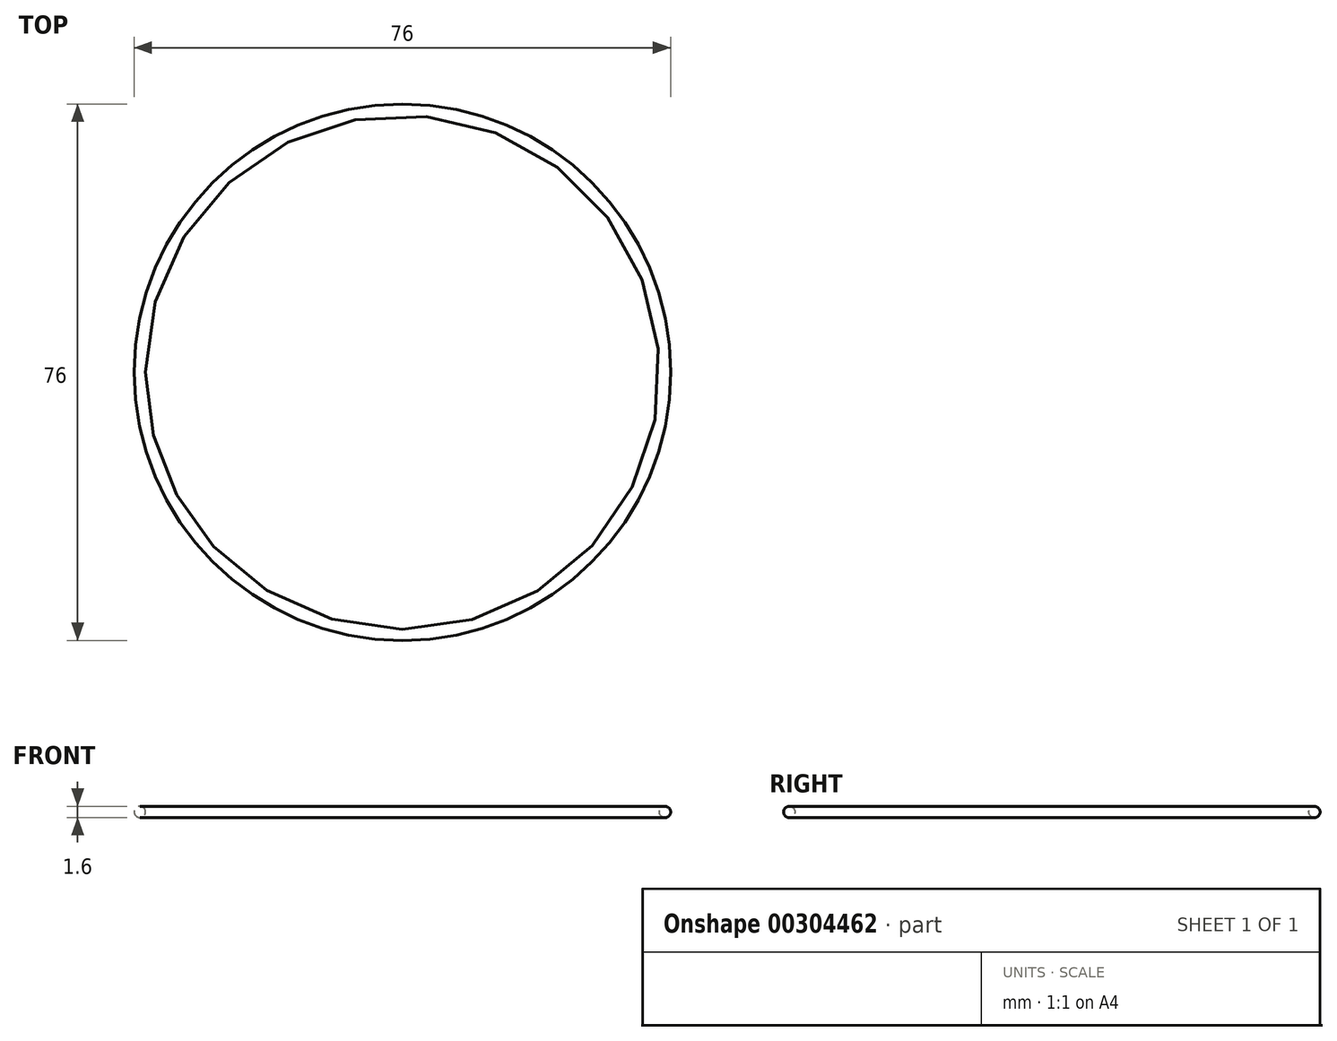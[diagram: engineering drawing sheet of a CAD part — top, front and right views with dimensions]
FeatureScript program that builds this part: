
annotation { "Feature Type Name" : "Feature", "Feature Type Description" : "" }
export const myFeature = defineFeature(function(context is Context, id is Id, definition is map)
    precondition{}
    {
        {
            var Q0;
            Q0=qCreatedBy(makeId("Front.planeOp"),FACE);
            var sketch = newSketch(context, id + "F0", { "sketchPlane" : qUnion([Q0])});
            skCircle(sketch, "E0", {"center": v(-37.2, 0) * mm, "radius": 0.8 * mm});
            skSolve(sketch);
        }
        {
            var Q0;
            Q0=qCreatedBy(makeId("Top.planeOp"),FACE);
            var sketch = newSketch(context, id + "F1", { "sketchPlane" : qUnion([Q0])});
            skCircle(sketch, "E1", {"center": v(0, 0) * mm, "radius": 37.2 * mm, "construction": true});
            skSolve(sketch);
        }
        {
            var Q0;
            Q0=makeQuery(id+"F0.imprint","IMPRINT",FACE,{"disambiguationData":[TD([[makeQuery(id+"F0.imprint","IMPRINT",EDGE,{"derivedFrom":sQuery(id+"F0.wireOp",EDGE,"E0")}),1.0]])]});
            var Q1;
            Q1=sQuery(id+"F1.wireOp",EDGE,"E1");
            revolve(context, id + "F2", {"entities" : qUnion([Q0]), "axis" : qUnion([Q1]), "revolveType" : RevolveType.FULL});
        }
    });
